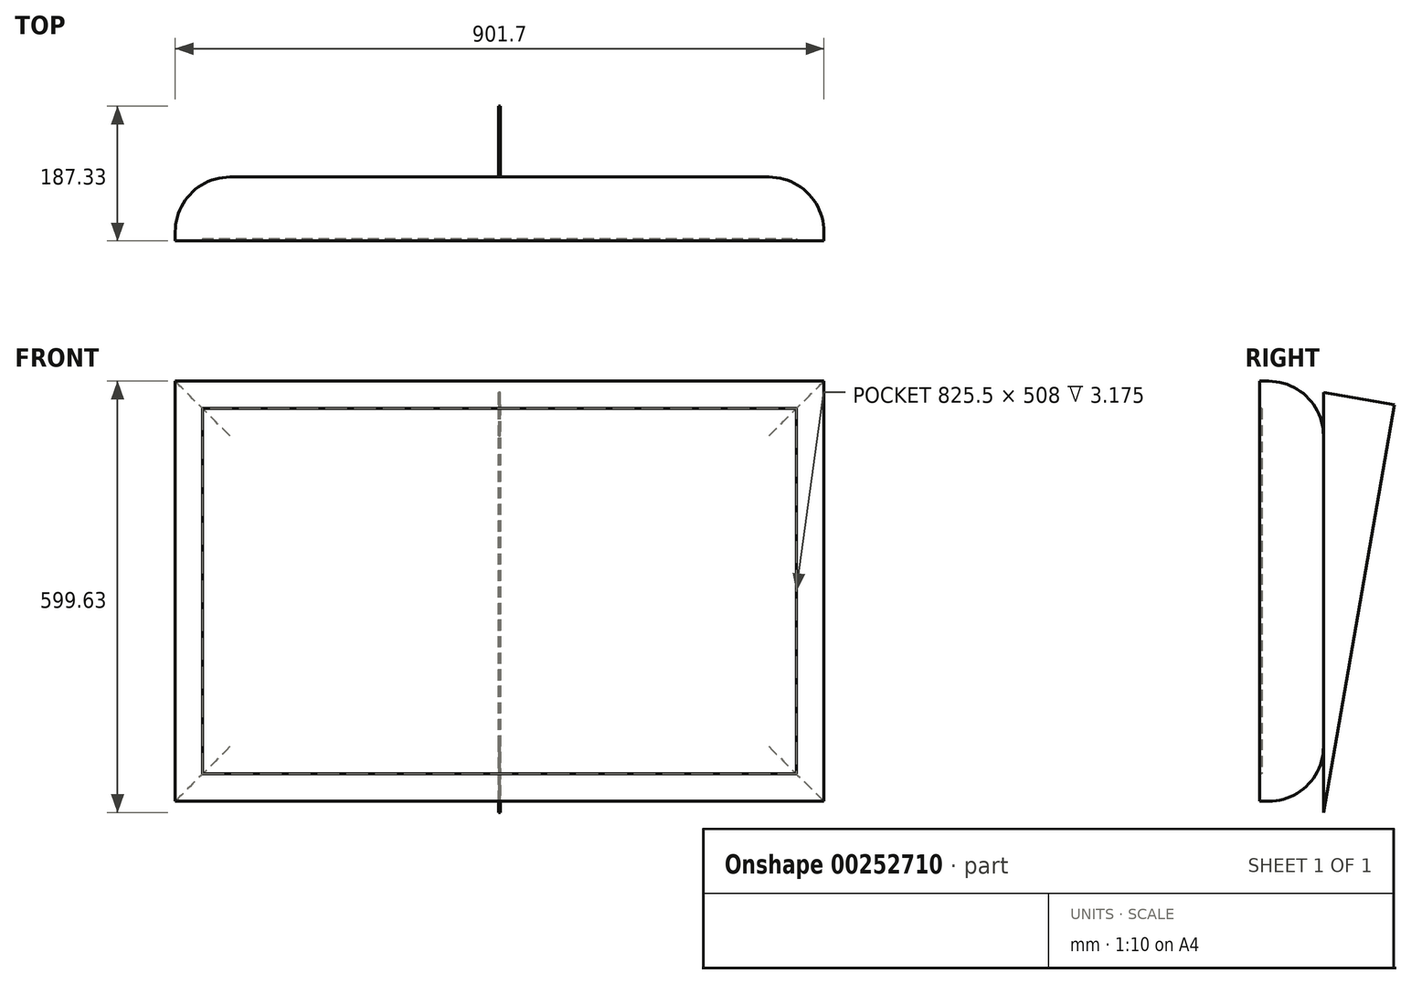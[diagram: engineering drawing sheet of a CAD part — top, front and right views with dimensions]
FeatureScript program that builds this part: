
annotation { "Feature Type Name" : "Feature", "Feature Type Description" : "" }
export const myFeature = defineFeature(function(context is Context, id is Id, definition is map)
    precondition{}
    {
        {
            var Q0;
            Q0=qCreatedBy(makeId("Front.planeOp"),FACE);
            var sketch = newSketch(context, id + "F0", { "sketchPlane" : qUnion([Q0])});
            skLineSegment(sketch, "E0.bottom", {"start": v(-450.85, 292.1) * mm, "end": v(450.85, 292.1) * mm});
            skLineSegment(sketch, "E0.top", {"start": v(-450.85, -292.1) * mm, "end": v(450.85, -292.1) * mm});
            skLineSegment(sketch, "E0.left", {"start": v(-450.85, 292.1) * mm, "end": v(-450.85, -292.1) * mm});
            skLineSegment(sketch, "E0.right", {"start": v(450.85, 292.1) * mm, "end": v(450.85, -292.1) * mm});
            skPoint(sketch, "E0.middle", {"position": v(0, 0) * mm});
            skSolve(sketch);
        }
        {
            var Q0;
            Q0 = qSketchRegion(id + "F0", true);
            extrude(context, id + "F1", {"entities" : qUnion([Q0]), "oppositeDirection" : true, "depth" : 88.9 * mm});
        }
        {
            var Q0;
            Q0=makeQuery(id+"F1.opExtrude","CAP_FACE",FACE,{"disambiguationData":[OSD([sQuery(id+"F0.wireOp",EDGE,"E0.bottom"),sQuery(id+"F0.wireOp",EDGE,"E0.top"),sQuery(id+"F0.wireOp",EDGE,"E0.left"),sQuery(id+"F0.wireOp",EDGE,"E0.right")])],"isStart":false});
            fillet(context, id + "F2", {"entities" : qUnion([Q0]), "radius" : 76.2 * mm, "tangentPropagation" : true, "allowEdgeOverflow" : false});
        }
        {
            var Q0;
            Q0=makeQuery(id+"F1.opExtrude","CAP_FACE",FACE,{"disambiguationData":[OSD([sQuery(id+"F0.wireOp",EDGE,"E0.bottom"),sQuery(id+"F0.wireOp",EDGE,"E0.top"),sQuery(id+"F0.wireOp",EDGE,"E0.left"),sQuery(id+"F0.wireOp",EDGE,"E0.right")])],"isStart":true});
            var sketch = newSketch(context, id + "F3", { "sketchPlane" : qUnion([Q0])});
            skPoint(sketch, "E1.middle", {"position": v(0, 0) * mm});
            skLineSegment(sketch, "E2.0", {"start": v(-412.75, 254) * mm, "end": v(-412.75, -254) * mm});
            skLineSegment(sketch, "E2.1", {"start": v(-412.75, 254) * mm, "end": v(412.75, 254) * mm});
            skLineSegment(sketch, "E2.2", {"start": v(412.75, -254) * mm, "end": v(412.75, 254) * mm});
            skLineSegment(sketch, "E2.3", {"start": v(-412.75, -254) * mm, "end": v(412.75, -254) * mm});
            skSolve(sketch);
        }
        {
            var Q0;
            Q0 = qSketchRegion(id + "F3", true);
            extrude(context, id + "F4", {"entities" : qUnion([Q0]), "operationType" : NewBodyOperationType.REMOVE, "oppositeDirection" : true, "depth" : 3.17 * mm});
        }
        {
            var Q0;
            Q0=qCreatedBy(makeId("Right.planeOp"),FACE);
            var sketch = newSketch(context, id + "F5", { "sketchPlane" : qUnion([Q0])});
            skLineSegment(sketch, "E3", {"start": v(187.32, 259.59) * mm, "end": v(88.9, -307.53) * mm});
            skLineSegment(sketch, "E4", {"start": v(88.9, -307.53) * mm, "end": v(88.9, -307.53) * mm});
            skLineSegment(sketch, "E5", {"start": v(88.9, -307.53) * mm, "end": v(88.9, 276.67) * mm});
            skLineSegment(sketch, "E6", {"start": v(187.33, 259.59) * mm, "end": v(88.9, 276.67) * mm});
            skSolve(sketch);
        }
        {
            var Q0;
            Q0 = qSketchRegion(id + "F5", true);
            extrude(context, id + "F6", {"entities" : qUnion([Q0]), "operationType" : NewBodyOperationType.ADD, "endBound" : BoundingType.SYMMETRIC, "depth" : 2.54 * mm});
        }
    });
